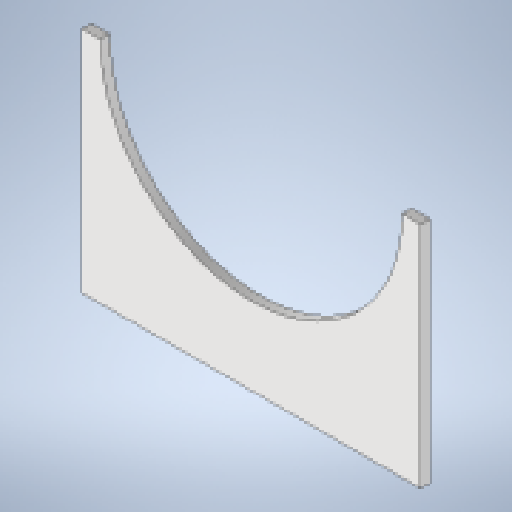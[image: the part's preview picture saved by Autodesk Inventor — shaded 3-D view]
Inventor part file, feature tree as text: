
AUTODESK INVENTOR PART (.ipt)
format: ipt  version: 2025 (Build 290162010, 162A)  size: 242,688 bytes
history: native  units: mm
features: sheet_metal_op x1, sketch x1, other x1
ambient origin geometry x8: Origin, YZ Plane, XZ Plane, XY Plane, X Axis, Y Axis, Z Axis, Center Point
bodies: Body1 (feature_tree)
feature tree (3):
  sheet_metal_op  "Face1"
  sketch  "Sketch1"  dims[d46=342.0mm d47=20.0mm d49=250.0mm d50=10.0mm]
  other  "Plate1"
